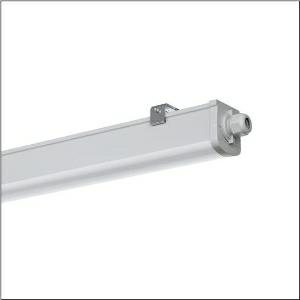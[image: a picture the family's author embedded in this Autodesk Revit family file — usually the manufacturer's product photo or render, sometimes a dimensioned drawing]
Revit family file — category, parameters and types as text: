
# Revit family: monsun_31_51fa20dp430b
name_source: partatom
category: Lighting Fixtures
units: mm (PartAtom-declared; Revit-internal decimal feet)

## family parameters
Cut with Voids When Loaded = No
Host = Face
Light Source = No
Part Type = Normal
Room Calculation Point = No
Round Connector Dimension = Use Diameter
Shared = No

## types (1)
- Monsun 31 (1 x LED, 3800 lm, 28 W, 4000K)
    Apparent Load = 28 VA
    CIE Flux Codes = 42 72 91 92 100
    Color Rendering = 80
    Color Temperature = 4000K
    Default Elevation = 1800 mm
    Description = Monsun 31, damp-proof luminaire, primary optical cover: diffuser, of PC, frosted, light emission: direct distribution, primary light characteristic: symmetric, installation type: surface-mounted, LED, rated luminous flux: 3.800lm, luminous efficacy: 136lm/W, light colour: 840, colour temperature: 4000K, control gear: DALI 2, with terminal, 5+1-pole, max. 2.5mm², through-wiring: 3x 2.5mm² + 3x 1.5mm², mains connection: 220..240V, AC, 50/60Hz, rated input power: 28W, housing, luminaire housing, of PC, light grey (RAL 7035), length: 1.458mm, width: 68mm, height: 76mm, protection rating (complete): IP66, insulation class (complete): insulation class II (safety insulation), certification: CE, ENEC, UKCA, protection symbol: D, impact resistance: IK08, permissible operating ambient temperature: -20..+40°C, corresponds to IFS (International Featured Standards) requirements for safety and quality in the food industry, contact your sales advisor before using the luminaires in applications with unclear chemical exposure, large temperature fluctuations or condensation-forming humidity, packaging unit: 1 piece
    Height = 77 mm
    Lamp = 1 x LED
    Lamp Light Flux = 3800 lm
    Lamp Power = 28 W
    Lamp count = 1
    Length = 1518 mm
    Luminous efficacy = 136 lm/W
    Manufacturer = Siteco
    ModVariant = No
    Model = 51FA20DP430B
    Mounting Place = Ceiling
    Mounting Type = Surface mounted
    Number of Poles = 1
    OnlyDefault = Yes
    Power Factor = 1
    Product Name = Monsun 31
    Product group = damp-proof luminaire
    ProductGroupID = 300
    Protection Class = Protection class II
    Protection Degree = IP 66
    RLX_Detail_Level = 1
    RLX_Emergency_Light_Flux = 0 lm
    RLX_Emergency_Type = 0
    RLX_Emergency_Type_DB = No
    RlxData = <blob elided: 33009 chars, md5=81b521ec>
    Socket = socket
    Standby Power = 0 W
    System Light Flux = 3800 lm
    System Power = 28 W
    Type Comments = Product without accessories
    Type Image = l_1006174.jpg
    URL = http://relux.com
    VarID = ---
    Voltage = 0 V
    Weight = 0.00 kg
    Width = 69 mm

## geometry (parser evidence)
native form markers: Blend x4, Sweep x12
no freeform markers — native parametric forms only
